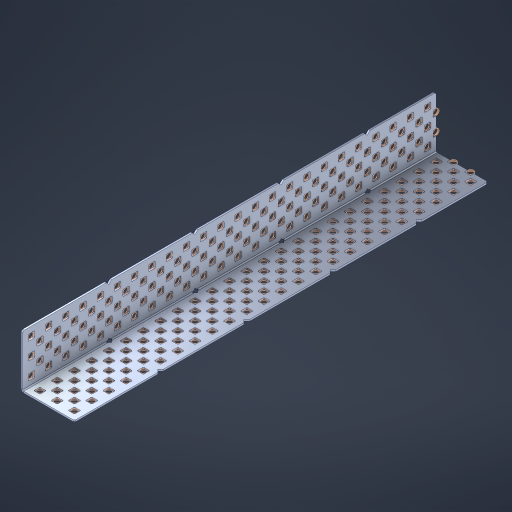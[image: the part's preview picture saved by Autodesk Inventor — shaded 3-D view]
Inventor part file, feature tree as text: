
AUTODESK INVENTOR PART (.ipt)
format: ipt  version: 2023 (Build 270158000, 158)  size: 2,503,680 bytes
history: native  units: in
note: dims shown in document units (in); Inventor stores cm internally (conversion verified against a paired STEP export)
features: other x246, extrude x238, sheet_metal_op x8, sketch x7, pattern_linear x3, mirror x1, chamfer x1
ambient origin geometry x8: Origin, YZ Plane, XZ Plane, XY Plane, X Axis, Y Axis, Z Axis, Center Point
bodies: Solid1 (feature_tree), Body (feature_tree)
feature tree (504):
  sheet_metal_op  "Flanges"
  sheet_metal_op  "Body Pattern"
  pattern_linear  "Center Double"  Spacing1=1.5in  [1 undecoded]
  pattern_linear  "Center Pattern"  Spacing1=0.1875in  [1 undecoded]
  other  "Arc Length"
  pattern_linear  "Notch Pattern"  Spacing1=0.0469in  [1 undecoded]
  other  "Diagonal Plane"
  mirror  "Everything Mirrored"
  chamfer  "End Chamfer"
  sketch  "Sketch1"  dims[d0=1.5in]
  other  "Plate1"
  sketch  "Sketch2"  dims[d1=12.0in]
  other  "Plate2"
  sheet_metal_op  "Bend1"
  sheet_metal_op  "Corner1"
  sketch  "Sketch8"  dims[d2=0.0469in]
  sketch  "Sketch9"  dims[d3=0.0469in]
  other  "Srf91"
  sheet_metal_op  "Body Pattern Sketch"
  other  "Srf92"
  sketch  "Sketch13"  dims[d4=0.0234in]
  sketch  "Sketch15"  dims[d5=0.0938in]
  sketch  "Sketch16"  dims[d6=0.0469in d7=1.5in d8=90.0deg d9=0.0312in d10=0.1875in d11=0.0469in d12=0.0469in d49=0.182in d50=0.02in d52=0.25in d53=0.0469in d54=0.0in d55=0.172in d56=1.0in d57=0.0in d85=0.1473in d86=0.1659in d89=0.0469in d90=0.0in d91=0.04in d92=0.0491in d95=2.5in d96=0.04in d97=0.25in d98=45.0deg d106=0.182in d107=0.02in d110=0.0469in d111=0.0in d112=0.172in d113=0.5in d114=0.0in d117=0.5in d126=0.0491in d127=0.1227in d128=0.08in d129=0.04in d130=2.5in d131=0.25in d132=9.4488in d134=0.5in d135=1.1811in d137=0.5in d140=0.5in d141=1.0in d142=0.3937in d144=0.5in d145=0.071in d146=0.7874in d148=0.5in]
  other  "Srf786"
  other  "Srf856"
  other  "Srf889"
  other  "Srf890"
  other  "Srf891"
  other  "Srf1275"
  other  "Srf1276"
  other  "Srf1278"
  other  "Srf1277"
  other  "Srf1285"
  other  "Srf1286"
  other  "Srf1287"
  other  "Srf1445"
  other  "Srf1446"
  other  "Srf1447"
  other  "Srf1448"
  other  "Srf1449"
  other  "Srf1537"
  other  "Srf1538"
  other  "Srf1539"
  other  "Srf1540"
  other  "Srf1541"
  other  "Srf1807"
  other  "Srf1808"
  other  "Srf1809"
  other  "Srf1810"
  other  "Srf1811"
  other  "Srf1812"
  other  "Srf1813"
  other  "Srf1814"
  other  "Srf1815"
  other  "Srf1816"
  other  "Srf1817"
  other  "Srf1818"
  other  "Srf1819"
  other  "Srf1820"
  other  "Srf1821"
  other  "Srf1959"
  other  "Srf1960"
  other  "Srf1961"
  other  "Srf1962"
  other  "Srf1963"
  other  "Srf1964"
  other  "Srf1965"
  other  "Srf1966"
  other  "Srf1967"
  other  "Srf1968"
  other  "Srf1969"
  other  "Srf1970"
  other  "Srf1971"
  other  "Srf1972"
  other  "Srf1973"
  other  "Srf2009"
  other  "Srf2010"
  other  "Srf2011"
  other  "Srf2012"
  other  "Srf2013"
  other  "Srf2014"
  other  "Srf2015"
  other  "Srf2016"
  other  "Srf2017"
  other  "Srf2018"
  other  "Srf2019"
  other  "Srf2020"
  other  "Srf2021"
  other  "Srf2022"
  other  "Srf2023"
  other  "Srf2024"
  other  "Srf2025"
  other  "Srf2026"
  other  "Srf2027"
  other  "Srf2028"
  other  "Srf2029"
  other  "Srf2030"
  other  "Srf2031"
  other  "Srf2032"
  other  "Srf2043"
  other  "Srf2044"
  other  "Srf2045"
  other  "Srf2046"
  other  "Srf2047"
  other  "Srf2048"
  other  "Srf2049"
  other  "Srf2050"
  other  "Srf2051"
  other  "Srf2052"
  other  "Srf2053"
  other  "Srf2054"
  other  "Srf2055"
  other  "Srf2056"
  other  "Srf2057"
  other  "Srf2058"
  other  "Srf2059"
  other  "Srf2060"
  other  "Srf2061"
  other  "Srf2062"
  other  "Srf2063"
  other  "Srf2064"
  other  "Srf2065"
  other  "Srf2076"
  other  "Srf2077"
  other  "Srf2078"
  other  "Srf2079"
  other  "Srf2080"
  other  "Srf2081"
  other  "Srf2082"
  other  "Srf2083"
  other  "Srf2084"
  other  "Srf2085"
  other  "Srf2086"
  other  "Srf2087"
  other  "Srf2088"
  other  "Srf2089"
  other  "Srf2090"
  other  "Srf2091"
  other  "Srf2092"
  other  "Srf2093"
  other  "Srf2094"
  other  "Srf2095"
  other  "Srf2096"
  other  "Srf2097"
  other  "Srf2098"
  other  "Srf2099"
  other  "Srf2100"
  other  "Srf2101"
  other  "Srf2102"
  other  "Srf2103"
  other  "Srf2104"
  other  "Srf2105"
  other  "Srf2106"
  other  "Srf2107"
  other  "Srf2108"
  other  "Srf2109"
  other  "Srf2110"
  other  "Srf2111"
  other  "Srf2112"
  other  "Srf2113"
  other  "Srf2114"
  other  "Srf2115"
  other  "Srf2116"
  other  "Srf2117"
  other  "Srf2118"
  other  "Srf2119"
  other  "Srf2120"
  other  "Srf2121"
  other  "Srf2122"
  other  "Srf2123"
  other  "Srf2124"
  other  "Srf2125"
  other  "Srf2126"
  other  "Srf2127"
  other  "Srf2128"
  other  "Srf2129"
  other  "Srf2130"
  other  "Srf2131"
  other  "Srf2132"
  other  "Srf2133"
  other  "Srf2134"
  other  "Srf2135"
  other  "Srf2136"
  other  "Srf2137"
  other  "Srf2138"
  other  "Srf2139"
  other  "Srf2140"
  other  "Srf2141"
  other  "Srf2142"
  other  "Srf2143"
  other  "Srf2144"
  other  "Srf2145"
  other  "Srf2179"
  other  "Srf2180"
  other  "Srf2181"
  other  "Srf2182"
  other  "Srf2183"
  other  "Srf2184"
  other  "Srf2185"
  other  "Srf2186"
  other  "Srf2187"
  other  "Srf2188"
  other  "Srf2189"
  other  "Srf2190"
  other  "Srf2191"
  other  "Srf2192"
  other  "Srf2193"
  other  "Srf2194"
  other  "Srf2195"
  other  "Srf2196"
  other  "Srf2197"
  other  "Srf2198"
  other  "Srf2199"
  other  "Srf2200"
  other  "Srf2201"
  other  "Srf2202"
  other  "Srf2203"
  other  "Srf2204"
  other  "Srf2205"
  other  "Srf2206"
  other  "Srf2207"
  other  "Srf2208"
  other  "Srf2209"
  other  "Srf2210"
  other  "Srf2211"
  other  "Srf2212"
  other  "Srf2213"
  other  "Srf2214"
  other  "Srf2215"
  other  "Srf2216"
  other  "Srf2217"
  other  "Srf2218"
  other  "Srf2219"
  other  "Srf2220"
  other  "Srf2221"
  other  "Srf2222"
  other  "Srf2223"
  other  "Srf2224"
  other  "Srf2225"
  other  "Srf2226"
  other  "Srf2227"
  other  "Srf2228"
  other  "Srf2229"
  other  "Srf2230"
  other  "Srf2231"
  other  "Srf2232"
  other  "Srf2233"
  other  "Srf2234"
  other  "Srf2235"
  other  "Srf2236"
  other  "Srf2237"
  other  "Srf2238"
  other  "Srf2239"
  other  "Srf2240"
  other  "Srf2241"
  other  "Srf2242"
  other  "Srf2243"
  other  "Srf2244"
  other  "Srf2245"
  other  "Srf2246"
  other  "Srf2247"
  sheet_metal_op  "Body Stamp"
  sheet_metal_op  "Body Circle"
  other  "Center Stamp"
  other  "Center Circle"
  sheet_metal_op  "Notch"
  extrude  "ExtrusionSrf92"  Depth=0.0469in
  extrude  "ExtrusionSrf856"  Depth=0.182in
  extrude  "ExtrusionSrf889"  Depth=0.02in
  extrude  "ExtrusionSrf890"  Depth=0.25in
  extrude  "ExtrusionSrf891"  Depth=0.0469in
  extrude  "ExtrusionSrf1275"  TaperAngle=0.0deg  [1 undecoded]
  extrude  "ExtrusionSrf1276"  Depth=0.5in
  extrude  "ExtrusionSrf1277"  Depth=1.0in TaperAngle=0.0deg
  extrude  "ExtrusionSrf1345"  Depth=0.5in
  extrude  "ExtrusionSrf1346"  Depth=0.5in
  extrude  "ExtrusionSrf1347"  Depth=0.0469in
  extrude  "ExtrusionSrf1348"  Depth=0.5in TaperAngle=0.0deg
  extrude  "ExtrusionSrf1445"  Depth=0.5in
  extrude  "ExtrusionSrf1446"  Depth=0.25in TaperAngle=45.0deg
  extrude  "ExtrusionSrf1447"  Depth=0.182in
  extrude  "ExtrusionSrf1448"  Depth=0.02in
  extrude  "ExtrusionSrf1449"  Depth=0.0469in
  extrude  "ExtrusionSrf1537"  TaperAngle=0.0deg  [1 undecoded]
  extrude  "ExtrusionSrf1538"  Depth=0.5in
  extrude  "ExtrusionSrf1539"  Depth=0.5in TaperAngle=0.0deg
  extrude  "ExtrusionSrf1540"  Depth=0.5in
  extrude  "ExtrusionSrf1541"  Depth=0.5in
  extrude  "ExtrusionSrf1807"  Depth=0.5in
  extrude  "ExtrusionSrf1808"  Depth=0.5in
  extrude  "ExtrusionSrf1809"  Depth=0.5in
  extrude  "ExtrusionSrf1810"  Depth=0.5in
  extrude  "ExtrusionSrf1811"  Depth=0.25in
  extrude  "ExtrusionSrf1812"  Depth=0.5in
  extrude  "ExtrusionSrf1813"  Depth=0.5in
  extrude  "ExtrusionSrf1814"  Depth=0.5in
  extrude  "ExtrusionSrf1815"  Depth=1.0in
  extrude  "ExtrusionSrf1816"  Depth=0.3937in
  extrude  "ExtrusionSrf1817"  Depth=0.5in
  extrude  "ExtrusionSrf1818"  Depth=0.5in
  extrude  "ExtrusionSrf1819"  [1 undecoded]
  extrude  "ExtrusionSrf1820"  [1 undecoded]
  extrude  "ExtrusionSrf1821"  [1 undecoded]
  extrude  "ExtrusionSrf1959"  [1 undecoded]
  extrude  "ExtrusionSrf1960"  [1 undecoded]
  extrude  "ExtrusionSrf1961"  [1 undecoded]
  extrude  "ExtrusionSrf1962"  [1 undecoded]
  extrude  "ExtrusionSrf1963"  [1 undecoded]
  extrude  "ExtrusionSrf1964"  [1 undecoded]
  extrude  "ExtrusionSrf1965"  [1 undecoded]
  extrude  "ExtrusionSrf1966"  [1 undecoded]
  extrude  "ExtrusionSrf1967"  [1 undecoded]
  extrude  "ExtrusionSrf1968"  [1 undecoded]
  extrude  "ExtrusionSrf1969"  [1 undecoded]
  extrude  "ExtrusionSrf1970"  [1 undecoded]
  extrude  "ExtrusionSrf1971"  [1 undecoded]
  extrude  "ExtrusionSrf1972"  [1 undecoded]
  extrude  "ExtrusionSrf1973"  [1 undecoded]
  extrude  "ExtrusionSrf2009"  [1 undecoded]
  extrude  "ExtrusionSrf2010"  [1 undecoded]
  extrude  "ExtrusionSrf2011"  [1 undecoded]
  extrude  "ExtrusionSrf2012"  [1 undecoded]
  extrude  "ExtrusionSrf2013"  [1 undecoded]
  extrude  "ExtrusionSrf2014"  [1 undecoded]
  extrude  "ExtrusionSrf2015"  [1 undecoded]
  extrude  "ExtrusionSrf2016"  [1 undecoded]
  extrude  "ExtrusionSrf2017"  [1 undecoded]
  extrude  "ExtrusionSrf2018"  [1 undecoded]
  extrude  "ExtrusionSrf2019"  [1 undecoded]
  extrude  "ExtrusionSrf2020"  [1 undecoded]
  extrude  "ExtrusionSrf2021"  [1 undecoded]
  extrude  "ExtrusionSrf2022"  [1 undecoded]
  extrude  "ExtrusionSrf2023"  [1 undecoded]
  extrude  "ExtrusionSrf2024"  [1 undecoded]
  extrude  "ExtrusionSrf2025"  [1 undecoded]
  extrude  "ExtrusionSrf2026"  [1 undecoded]
  extrude  "ExtrusionSrf2027"  [1 undecoded]
  extrude  "ExtrusionSrf2028"  [1 undecoded]
  extrude  "ExtrusionSrf2029"  [1 undecoded]
  extrude  "ExtrusionSrf2030"  [1 undecoded]
  extrude  "ExtrusionSrf2031"  [1 undecoded]
  extrude  "ExtrusionSrf2032"  [1 undecoded]
  extrude  "ExtrusionSrf2043"  [1 undecoded]
  extrude  "ExtrusionSrf2044"  [1 undecoded]
  extrude  "ExtrusionSrf2045"  [1 undecoded]
  extrude  "ExtrusionSrf2046"  [1 undecoded]
  extrude  "ExtrusionSrf2047"  [1 undecoded]
  extrude  "ExtrusionSrf2048"  [1 undecoded]
  extrude  "ExtrusionSrf2049"  [1 undecoded]
  extrude  "ExtrusionSrf2050"  [1 undecoded]
  extrude  "ExtrusionSrf2051"  [1 undecoded]
  extrude  "ExtrusionSrf2052"  [1 undecoded]
  extrude  "ExtrusionSrf2053"  [1 undecoded]
  extrude  "ExtrusionSrf2054"  [1 undecoded]
  extrude  "ExtrusionSrf2055"  [1 undecoded]
  extrude  "ExtrusionSrf2056"  [1 undecoded]
  extrude  "ExtrusionSrf2057"  [1 undecoded]
  extrude  "ExtrusionSrf2058"  [1 undecoded]
  extrude  "ExtrusionSrf2059"  [1 undecoded]
  extrude  "ExtrusionSrf2060"  [1 undecoded]
  extrude  "ExtrusionSrf2061"  [1 undecoded]
  extrude  "ExtrusionSrf2062"  [1 undecoded]
  extrude  "ExtrusionSrf2063"  [1 undecoded]
  extrude  "ExtrusionSrf2064"  [1 undecoded]
  extrude  "ExtrusionSrf2065"  [1 undecoded]
  extrude  "ExtrusionSrf2076"  [1 undecoded]
  extrude  "ExtrusionSrf2077"  [1 undecoded]
  extrude  "ExtrusionSrf2078"  [1 undecoded]
  extrude  "ExtrusionSrf2079"  [1 undecoded]
  extrude  "ExtrusionSrf2080"  [1 undecoded]
  extrude  "ExtrusionSrf2081"  [1 undecoded]
  extrude  "ExtrusionSrf2082"  [1 undecoded]
  extrude  "ExtrusionSrf2083"  [1 undecoded]
  extrude  "ExtrusionSrf2084"  [1 undecoded]
  extrude  "ExtrusionSrf2085"  [1 undecoded]
  extrude  "ExtrusionSrf2086"  [1 undecoded]
  extrude  "ExtrusionSrf2087"  [1 undecoded]
  extrude  "ExtrusionSrf2088"  [1 undecoded]
  extrude  "ExtrusionSrf2089"  [1 undecoded]
  extrude  "ExtrusionSrf2090"  [1 undecoded]
  extrude  "ExtrusionSrf2091"  [1 undecoded]
  extrude  "ExtrusionSrf2092"  [1 undecoded]
  extrude  "ExtrusionSrf2093"  [1 undecoded]
  extrude  "ExtrusionSrf2094"  [1 undecoded]
  extrude  "ExtrusionSrf2095"  [1 undecoded]
  extrude  "ExtrusionSrf2096"  [1 undecoded]
  extrude  "ExtrusionSrf2097"  [1 undecoded]
  extrude  "ExtrusionSrf2098"  [1 undecoded]
  extrude  "ExtrusionSrf2099"  [1 undecoded]
  extrude  "ExtrusionSrf2100"  [1 undecoded]
  extrude  "ExtrusionSrf2101"  [1 undecoded]
  extrude  "ExtrusionSrf2102"  [1 undecoded]
  extrude  "ExtrusionSrf2103"  [1 undecoded]
  extrude  "ExtrusionSrf2104"  [1 undecoded]
  extrude  "ExtrusionSrf2105"  [1 undecoded]
  extrude  "ExtrusionSrf2106"  [1 undecoded]
  extrude  "ExtrusionSrf2107"  [1 undecoded]
  extrude  "ExtrusionSrf2108"  [1 undecoded]
  extrude  "ExtrusionSrf2109"  [1 undecoded]
  extrude  "ExtrusionSrf2110"  [1 undecoded]
  extrude  "ExtrusionSrf2111"  [1 undecoded]
  extrude  "ExtrusionSrf2112"  [1 undecoded]
  extrude  "ExtrusionSrf2113"  [1 undecoded]
  extrude  "ExtrusionSrf2114"  [1 undecoded]
  extrude  "ExtrusionSrf2115"  [1 undecoded]
  extrude  "ExtrusionSrf2116"  [1 undecoded]
  extrude  "ExtrusionSrf2117"  [1 undecoded]
  extrude  "ExtrusionSrf2118"  [1 undecoded]
  extrude  "ExtrusionSrf2119"  [1 undecoded]
  extrude  "ExtrusionSrf2120"  [1 undecoded]
  extrude  "ExtrusionSrf2121"  [1 undecoded]
  extrude  "ExtrusionSrf2122"  [1 undecoded]
  extrude  "ExtrusionSrf2123"  [1 undecoded]
  extrude  "ExtrusionSrf2124"  [1 undecoded]
  extrude  "ExtrusionSrf2125"  [1 undecoded]
  extrude  "ExtrusionSrf2126"  [1 undecoded]
  extrude  "ExtrusionSrf2127"  [1 undecoded]
  extrude  "ExtrusionSrf2128"  [1 undecoded]
  extrude  "ExtrusionSrf2129"  [1 undecoded]
  extrude  "ExtrusionSrf2130"  [1 undecoded]
  extrude  "ExtrusionSrf2131"  [1 undecoded]
  extrude  "ExtrusionSrf2132"  [1 undecoded]
  extrude  "ExtrusionSrf2133"  [1 undecoded]
  extrude  "ExtrusionSrf2134"  [1 undecoded]
  extrude  "ExtrusionSrf2135"  [1 undecoded]
  extrude  "ExtrusionSrf2136"  [1 undecoded]
  extrude  "ExtrusionSrf2137"  [1 undecoded]
  extrude  "ExtrusionSrf2138"  [1 undecoded]
  extrude  "ExtrusionSrf2139"  [1 undecoded]
  extrude  "ExtrusionSrf2140"  [1 undecoded]
  extrude  "ExtrusionSrf2141"  [1 undecoded]
  extrude  "ExtrusionSrf2142"  [1 undecoded]
  extrude  "ExtrusionSrf2143"  [1 undecoded]
  extrude  "ExtrusionSrf2144"  [1 undecoded]
  extrude  "ExtrusionSrf2145"  [1 undecoded]
  extrude  "ExtrusionSrf2179"  [1 undecoded]
  extrude  "ExtrusionSrf2180"  [1 undecoded]
  extrude  "ExtrusionSrf2181"  [1 undecoded]
  extrude  "ExtrusionSrf2182"  [1 undecoded]
  extrude  "ExtrusionSrf2183"  [1 undecoded]
  extrude  "ExtrusionSrf2184"  [1 undecoded]
  extrude  "ExtrusionSrf2185"  [1 undecoded]
  extrude  "ExtrusionSrf2186"  [1 undecoded]
  extrude  "ExtrusionSrf2187"  [1 undecoded]
  extrude  "ExtrusionSrf2188"  [1 undecoded]
  extrude  "ExtrusionSrf2189"  [1 undecoded]
  extrude  "ExtrusionSrf2190"  [1 undecoded]
  extrude  "ExtrusionSrf2191"  [1 undecoded]
  extrude  "ExtrusionSrf2192"  [1 undecoded]
  extrude  "ExtrusionSrf2193"  [1 undecoded]
  extrude  "ExtrusionSrf2194"  [1 undecoded]
  extrude  "ExtrusionSrf2195"  [1 undecoded]
  extrude  "ExtrusionSrf2196"  [1 undecoded]
  extrude  "ExtrusionSrf2197"  [1 undecoded]
  extrude  "ExtrusionSrf2198"  [1 undecoded]
  extrude  "ExtrusionSrf2199"  [1 undecoded]
  extrude  "ExtrusionSrf2200"  [1 undecoded]
  extrude  "ExtrusionSrf2201"  [1 undecoded]
  extrude  "ExtrusionSrf2202"  [1 undecoded]
  extrude  "ExtrusionSrf2203"  [1 undecoded]
  extrude  "ExtrusionSrf2204"  [1 undecoded]
  extrude  "ExtrusionSrf2205"  [1 undecoded]
  extrude  "ExtrusionSrf2206"  [1 undecoded]
  extrude  "ExtrusionSrf2207"  [1 undecoded]
  extrude  "ExtrusionSrf2208"  [1 undecoded]
  extrude  "ExtrusionSrf2209"  [1 undecoded]
  extrude  "ExtrusionSrf2210"  [1 undecoded]
  extrude  "ExtrusionSrf2211"  [1 undecoded]
  extrude  "ExtrusionSrf2212"  [1 undecoded]
  extrude  "ExtrusionSrf2213"  [1 undecoded]
  extrude  "ExtrusionSrf2214"  [1 undecoded]
  extrude  "ExtrusionSrf2215"  [1 undecoded]
  extrude  "ExtrusionSrf2216"  [1 undecoded]
  extrude  "ExtrusionSrf2217"  [1 undecoded]
  extrude  "ExtrusionSrf2218"  [1 undecoded]
  extrude  "ExtrusionSrf2219"  [1 undecoded]
  extrude  "ExtrusionSrf2220"  [1 undecoded]
  extrude  "ExtrusionSrf2221"  [1 undecoded]
  extrude  "ExtrusionSrf2222"  [1 undecoded]
  extrude  "ExtrusionSrf2223"  [1 undecoded]
  extrude  "ExtrusionSrf2224"  [1 undecoded]
  extrude  "ExtrusionSrf2225"  [1 undecoded]
  extrude  "ExtrusionSrf2226"  [1 undecoded]
  extrude  "ExtrusionSrf2227"  [1 undecoded]
  extrude  "ExtrusionSrf2228"  [1 undecoded]
  extrude  "ExtrusionSrf2229"  [1 undecoded]
  extrude  "ExtrusionSrf2230"  [1 undecoded]
  extrude  "ExtrusionSrf2231"  [1 undecoded]
  extrude  "ExtrusionSrf2232"  [1 undecoded]
  extrude  "ExtrusionSrf2233"  [1 undecoded]
  extrude  "ExtrusionSrf2234"  [1 undecoded]
  extrude  "ExtrusionSrf2235"  [1 undecoded]
  extrude  "ExtrusionSrf2236"  [1 undecoded]
  extrude  "ExtrusionSrf2237"  [1 undecoded]
  extrude  "ExtrusionSrf2238"  [1 undecoded]
  extrude  "ExtrusionSrf2239"  [1 undecoded]
  extrude  "ExtrusionSrf2240"  [1 undecoded]
  extrude  "ExtrusionSrf2241"  [1 undecoded]
  extrude  "ExtrusionSrf2242"  [1 undecoded]
  extrude  "ExtrusionSrf2243"  [1 undecoded]
  extrude  "ExtrusionSrf2244"  [1 undecoded]
  extrude  "ExtrusionSrf2245"  [1 undecoded]
  extrude  "ExtrusionSrf2246"  [1 undecoded]
  extrude  "ExtrusionSrf2247"  [1 undecoded]
note: 209 required parameter values undecoded (feature->parameter linkage not recoverable at this tier; creation-order binding heuristic only, values carry confidence <= 0.55)
